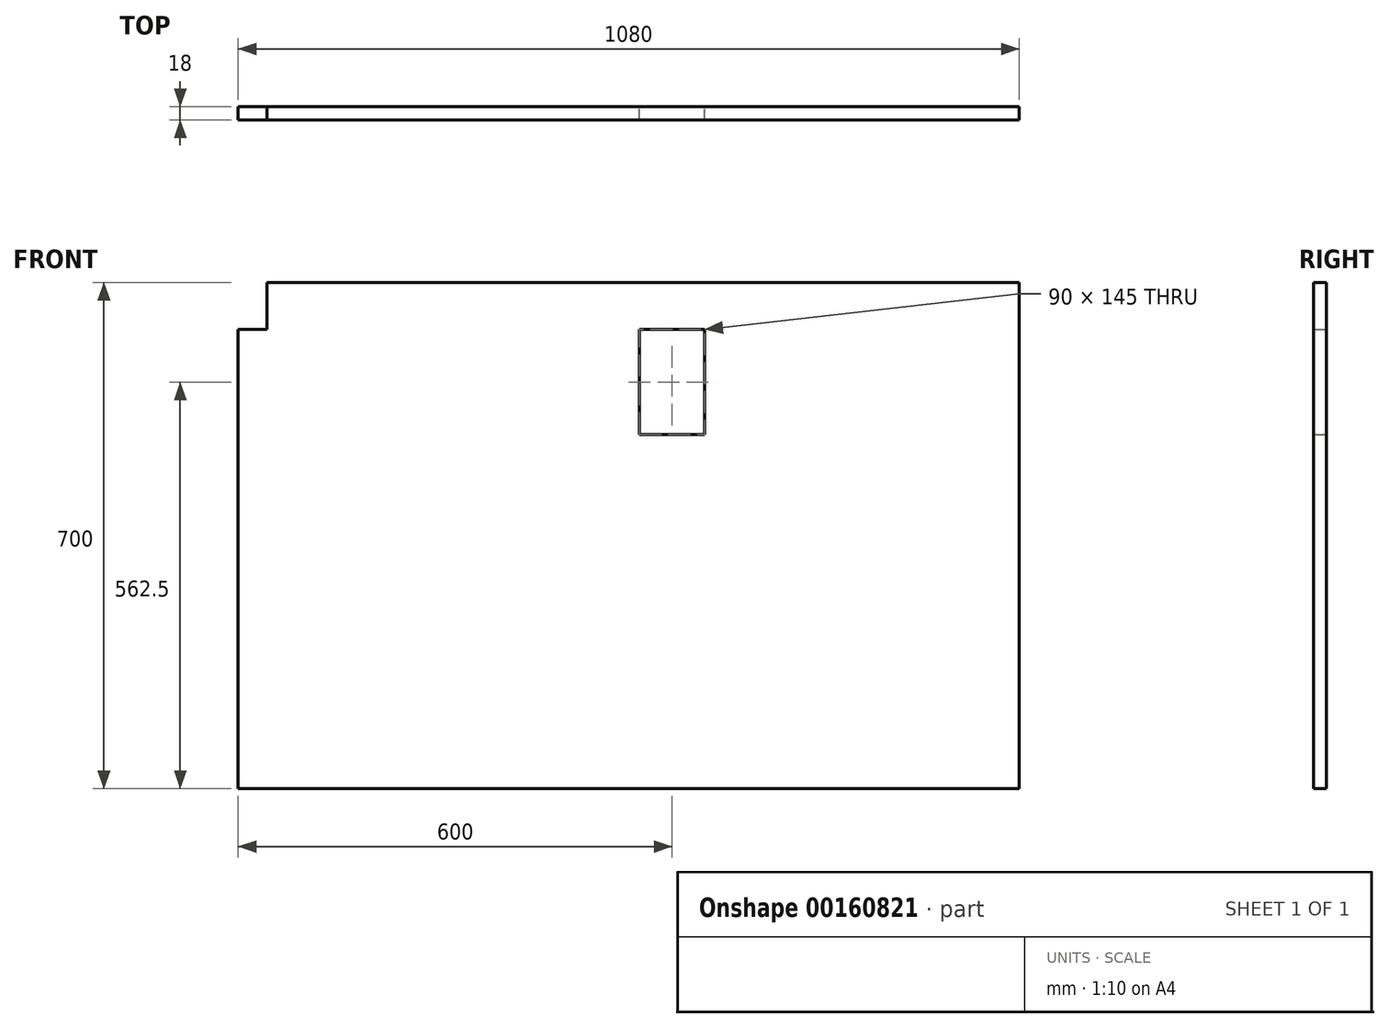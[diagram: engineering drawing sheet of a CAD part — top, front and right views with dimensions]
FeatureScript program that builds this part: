
annotation { "Feature Type Name" : "Feature", "Feature Type Description" : "" }
export const myFeature = defineFeature(function(context is Context, id is Id, definition is map)
    precondition{}
    {
        {
            var Q0;
            Q0=qCreatedBy(makeId("Front.planeOp"),FACE);
            var sketch = newSketch(context, id + "F0", { "sketchPlane" : qUnion([Q0])});
            skLineSegment(sketch, "E0.bottom", {"start": v(0, 0) * mm, "end": v(1080, 0) * mm});
            skLineSegment(sketch, "E0.top", {"start": v(40, 700) * mm, "end": v(1080, 700) * mm});
            skLineSegment(sketch, "E0.left", {"start": v(0, 0) * mm, "end": v(0, 635) * mm});
            skLineSegment(sketch, "E0.right", {"start": v(1080, 0) * mm, "end": v(1080, 700) * mm});
            skLineSegment(sketch, "E1.top", {"start": v(0, 635) * mm, "end": v(40, 635) * mm});
            skLineSegment(sketch, "E1.right", {"start": v(40, 700) * mm, "end": v(40, 635) * mm});
            skLineSegment(sketch, "E2.bottom", {"start": v(555, 635) * mm, "end": v(645, 635) * mm});
            skLineSegment(sketch, "E2.top", {"start": v(555, 490) * mm, "end": v(645, 490) * mm});
            skLineSegment(sketch, "E2.left", {"start": v(555, 635) * mm, "end": v(555, 490) * mm});
            skLineSegment(sketch, "E2.right", {"start": v(645, 635) * mm, "end": v(645, 490) * mm});
            skSolve(sketch);
        }
        {
            var Q0;
            Q0=qSketchRegion(id+"F0",true);
            extrude(context, id + "F1", {"entities" : qUnion([Q0]), "depth" : 18 * mm});
        }
    });
